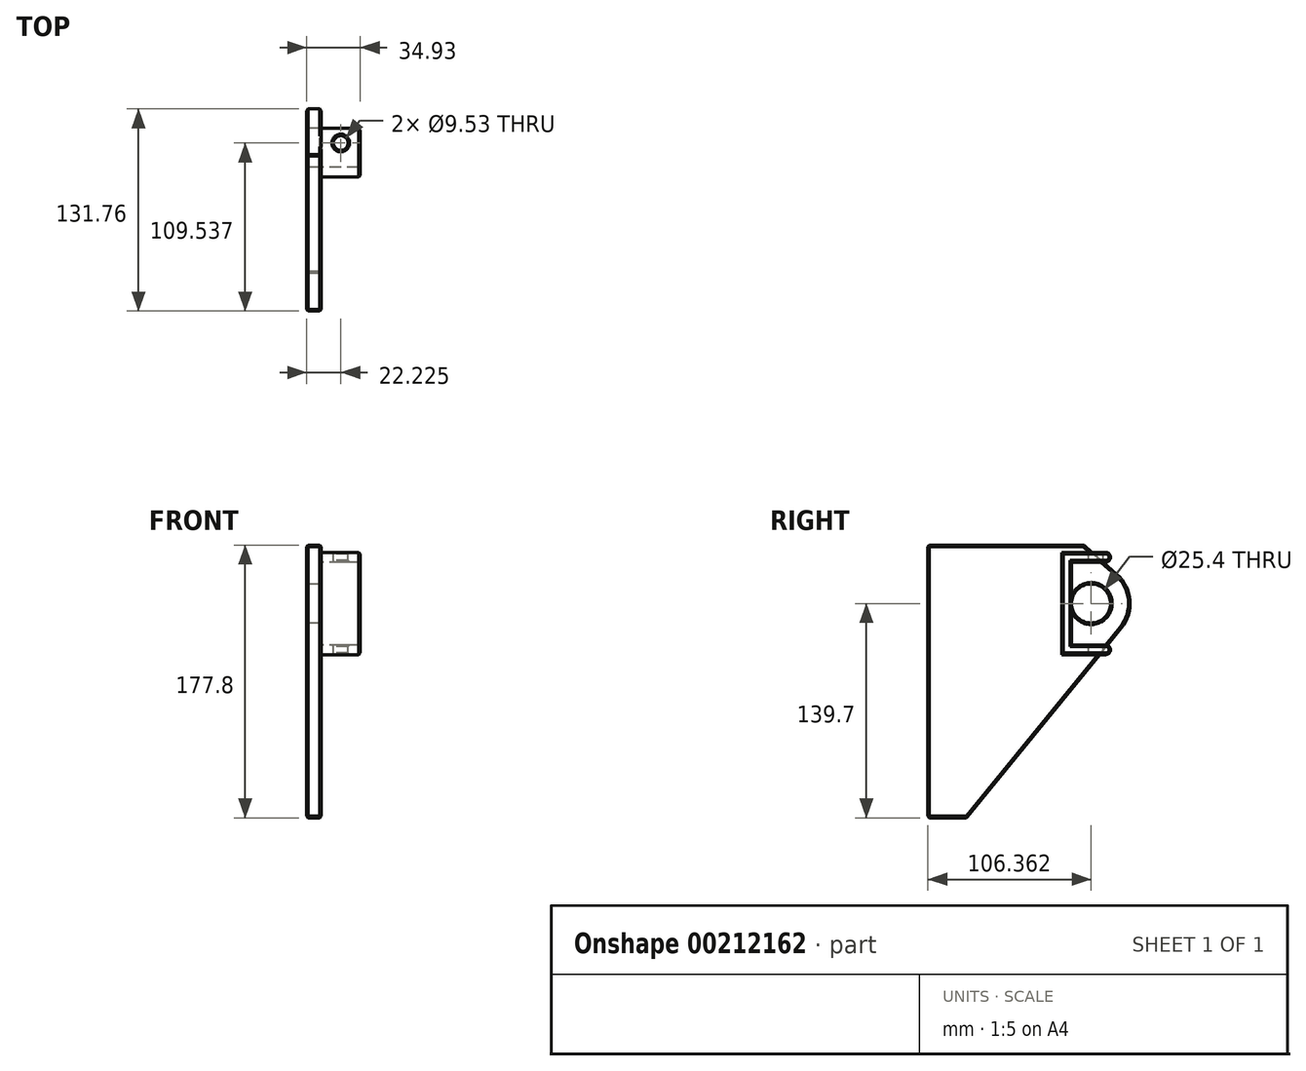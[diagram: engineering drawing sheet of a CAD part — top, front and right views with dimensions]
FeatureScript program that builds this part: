
annotation { "Feature Type Name" : "Feature", "Feature Type Description" : "" }
export const myFeature = defineFeature(function(context is Context, id is Id, definition is map)
    precondition{}
    {
        {
            var Q0;
            Q0=qCreatedBy(makeId("Right.planeOp"),FACE);
            var sketch = newSketch(context, id + "F0", { "sketchPlane" : qUnion([Q0])});
            skLineSegment(sketch, "E0", {"start": v(0, 0) * mm, "end": v(0, 177.8) * mm});
            skLineSegment(sketch, "E1", {"start": v(0, 177.8) * mm, "end": v(101.6, 177.8) * mm});
            skLineSegment(sketch, "E2", {"start": v(25.4, 0) * mm, "end": v(0, 0) * mm});
            skCircle(sketch, "E3", {"center": v(106.36, 139.7) * mm, "radius": 12.7 * mm});
            skLineSegment(sketch, "E4", {"start": v(25.4, 0) * mm, "end": v(126.06, 123.67) * mm});
            skLineSegment(sketch, "E5", {"start": v(101.6, 177.8) * mm, "end": v(123.18, 158.74) * mm});
            skArc(sketch, "E6", {"start": v(126.06, 123.67) * mm, "mid": v(131.68, 141.78) * mm, "end": v(123.18, 158.74) * mm});
            skSolve(sketch);
        }
        {
            var Q0;
            Q0=makeQuery(id+"F0.imprint","IMPRINT",FACE,{"disambiguationData":[TD([[makeQuery(id+"F0.imprint","IMPRINT",EDGE,{"derivedFrom":sQuery(id+"F0.wireOp",EDGE,"E0")}),-1.0]])]});
            extrude(context, id + "F1", {"entities" : qUnion([Q0]), "depth" : 9.52 * mm});
        }
        {
            var Q0;
            Q0=makeQuery(id+"F1.opExtrude","CAP_FACE",FACE,{"disambiguationData":[OSD([sQuery(id+"F0.wireOp",EDGE,"E0"),sQuery(id+"F0.wireOp",EDGE,"E1"),sQuery(id+"F0.wireOp",EDGE,"E2"),sQuery(id+"F0.wireOp",EDGE,"E3"),sQuery(id+"F0.wireOp",EDGE,"E4"),sQuery(id+"F0.wireOp",EDGE,"E5"),sQuery(id+"F0.wireOp",EDGE,"E6")])],"isStart":true});
            var sketch = newSketch(context, id + "F2", { "sketchPlane" : qUnion([Q0])});
            skLineSegment(sketch, "E7", {"start": v(-106.36, 139.7) * mm, "end": v(133.79, 139.7) * mm, "construction": true});
            skLineSegment(sketch, "E8", {"start": v(-106.36, 139.7) * mm, "end": v(-106.36, -37.97) * mm, "construction": true});
            skLineSegment(sketch, "E9", {"start": v(-106.36, 139.7) * mm, "end": v(-106.36, 193.68) * mm, "construction": true});
            skLineSegment(sketch, "E10", {"start": v(-131.76, 109.54) * mm, "end": v(-131.76, 109.54) * mm});
            skLineSegment(sketch, "E11", {"start": v(-135.09, 169.86) * mm, "end": v(-135.09, 169.86) * mm});
            skPoint(sketch, "E12.visualSharp", {"position": v(-135.09, 173.04) * mm});
            skPoint(sketch, "E13.visualSharp", {"position": v(-135.09, 166.69) * mm});
            skPoint(sketch, "E14.visualSharp", {"position": v(-131.76, 112.71) * mm});
            skPoint(sketch, "E15.visualSharp", {"position": v(-131.76, 106.36) * mm});
            skLineSegment(sketch, "E16", {"start": v(-93.66, 139.7) * mm, "end": v(-93.66, 166.69) * mm});
            skLineSegment(sketch, "E17", {"start": v(-93.66, 139.7) * mm, "end": v(-93.66, 112.71) * mm});
            skLineSegment(sketch, "E18.0", {"start": v(-87.31, 139.7) * mm, "end": v(-87.31, 173.04) * mm});
            skLineSegment(sketch, "E19.0", {"start": v(-87.31, 139.7) * mm, "end": v(-87.31, 106.36) * mm});
            skLineSegment(sketch, "E20", {"start": v(-87.31, 173.04) * mm, "end": v(-115.89, 173.04) * mm});
            skLineSegment(sketch, "E21.0", {"start": v(-93.66, 166.69) * mm, "end": v(-115.89, 166.69) * mm});
            skLineSegment(sketch, "E22", {"start": v(-87.31, 106.36) * mm, "end": v(-115.89, 106.36) * mm});
            skLineSegment(sketch, "E23.0", {"start": v(-93.66, 112.71) * mm, "end": v(-115.89, 112.71) * mm});
            skLineSegment(sketch, "E24", {"start": v(-119.06, 169.86) * mm, "end": v(-119.06, 169.86) * mm});
            skLineSegment(sketch, "E25", {"start": v(-119.06, 109.54) * mm, "end": v(-119.06, 109.54) * mm});
            skPoint(sketch, "E26.visualSharp", {"position": v(-119.06, 112.71) * mm});
            skArc(sketch, "E26.filletArc", {"start": v(-115.89, 112.71) * mm, "mid": v(-118.13, 111.78) * mm, "end": v(-119.06, 109.54) * mm});
            skPoint(sketch, "E27.visualSharp", {"position": v(-119.06, 106.36) * mm});
            skArc(sketch, "E27.filletArc", {"start": v(-119.06, 109.54) * mm, "mid": v(-118.13, 107.3) * mm, "end": v(-115.89, 106.36) * mm});
            skPoint(sketch, "E28.visualSharp", {"position": v(-119.06, 173.04) * mm});
            skArc(sketch, "E28.filletArc", {"start": v(-115.89, 173.04) * mm, "mid": v(-118.13, 172.1) * mm, "end": v(-119.06, 169.86) * mm});
            skPoint(sketch, "E29.visualSharp", {"position": v(-119.06, 166.69) * mm});
            skArc(sketch, "E29.filletArc", {"start": v(-119.06, 169.86) * mm, "mid": v(-118.13, 167.62) * mm, "end": v(-115.89, 166.69) * mm});
            skSolve(sketch);
        }
        {
            var Q0;
            {var subQ6=sQuery(id+"F2.wireOp",EDGE,"E16");Q0=makeQuery(id+"F2.imprint","IMPRINT",FACE,{"disambiguationData":[TD([[makeQuery(id+"F2.imprint","IMPRINT",EDGE,{"derivedFrom":subQ6}),-1.0]])]});}
            var Q1;
            {var subQ1=sQuery(id+"F2.wireOp",EDGE,"E28.filletArc");Q1=makeQuery(id+"F2.imprint","IMPRINT",FACE,{"disambiguationData":[TD([[makeQuery(id+"F2.imprint","IMPRINT",EDGE,{"derivedFrom":subQ1}),1.0]])]});}
            var Q2;
            {var subQ0=sQuery(id+"F2.wireOp",EDGE,"E27.filletArc");Q2=makeQuery(id+"F2.imprint","IMPRINT",FACE,{"disambiguationData":[TD([[makeQuery(id+"F2.imprint","IMPRINT",EDGE,{"derivedFrom":subQ0}),1.0]])]});}
            extrude(context, id + "F3", {"entities" : qUnion([Q0, Q1, Q2]), "operationType" : NewBodyOperationType.ADD, "oppositeDirection" : true, "depth" : 34.92 * mm, "hasSecondDirection" : true, "secondDirectionOppositeDirection" : true, "secondDirectionDepth" : 9.52 * mm});
        }
        {
            var Q0;
            Q0=makeQuery(id+"F3.opExtrude","SWEPT_FACE",FACE,{"disambiguationData":[OSD([sQuery(id+"F2.wireOp",EDGE,"E20")])]});
            var sketch = newSketch(context, id + "F4", { "sketchPlane" : qUnion([Q0])});
            skCircle(sketch, "E30", {"center": v(22.23, 109.54) * mm, "radius": 4.76 * mm});
            skSolve(sketch);
        }
        {
            var Q0;
            Q0=makeQuery(id+"F4.imprint","IMPRINT",FACE,{"disambiguationData":[TD([[makeQuery(id+"F4.imprint","IMPRINT",EDGE,{"derivedFrom":sQuery(id+"F4.wireOp",EDGE,"E30")}),1.0]])]});
            extrude(context, id + "F5", {"entities" : qUnion([Q0]), "operationType" : NewBodyOperationType.REMOVE, "endBound" : BoundingType.THROUGH_ALL, "oppositeDirection" : true, "depth" : 25.4 * mm});
        }
        {
            var Q0;
            Q0=makeQuery(id+"F1.opExtrude","CAP_FACE",FACE,{"disambiguationData":[OSD([sQuery(id+"F0.wireOp",EDGE,"E0"),sQuery(id+"F0.wireOp",EDGE,"E1"),sQuery(id+"F0.wireOp",EDGE,"E2"),sQuery(id+"F0.wireOp",EDGE,"E3"),sQuery(id+"F0.wireOp",EDGE,"E4"),sQuery(id+"F0.wireOp",EDGE,"E5"),sQuery(id+"F0.wireOp",EDGE,"E6")])],"isStart":true});
            var Q1;
            Q1=makeQuery(id+"F1.opExtrude","CAP_EDGE",EDGE,{"disambiguationData":[OSD([sQuery(id+"F0.wireOp",EDGE,"E3")])],"isStart":false});
            var Q2;
            Q2=makeQuery(id+"F1.opExtrude","CAP_EDGE",EDGE,{"disambiguationData":[OSD([sQuery(id+"F0.wireOp",EDGE,"E0")])],"isStart":false});
            var Q3;
            Q3=makeQuery(id+"F1.opExtrude","CAP_EDGE",EDGE,{"disambiguationData":[OSD([sQuery(id+"F0.wireOp",EDGE,"E2")])],"isStart":false});
            var Q4;
            {var subQ0=sQuery(id+"F2.wireOp",EDGE,"E22");var subQ1=sQuery(id+"F0.wireOp",EDGE,"E2");var subQ2=sQuery(id+"F0.wireOp",EDGE,"E4");Q4=makeQuery(id+"F3.boolean.opBoolean","SPLIT",EDGE,{"disambiguationData":[TD([makeQuery(id+"F1.opExtrude","CAP_FACE",FACE,{"disambiguationData":[OSD([sQuery(id+"F0.wireOp",EDGE,"E0"),sQuery(id+"F0.wireOp",EDGE,"E1"),subQ1,sQuery(id+"F0.wireOp",EDGE,"E3"),subQ2,sQuery(id+"F0.wireOp",EDGE,"E5"),sQuery(id+"F0.wireOp",EDGE,"E6")])],"isStart":false}),makeQuery(id+"F1.opExtrude","SWEPT_FACE",FACE,{"disambiguationData":[OSD([subQ1])]}),makeQuery(id+"F1.opExtrude","SWEPT_FACE",FACE,{"disambiguationData":[OSD([subQ2])]}),makeQuery(id+"F3.opExtrude","CAP_FACE",FACE,{"disambiguationData":[OSD([sQuery(id+"F2.wireOp",EDGE,"E16"),sQuery(id+"F2.wireOp",EDGE,"E17"),sQuery(id+"F2.wireOp",EDGE,"E18.0"),sQuery(id+"F2.wireOp",EDGE,"E19.0"),sQuery(id+"F2.wireOp",EDGE,"E20"),sQuery(id+"F2.wireOp",EDGE,"E21.0"),subQ0,sQuery(id+"F2.wireOp",EDGE,"E23.0"),sQuery(id+"F2.wireOp",EDGE,"E26.filletArc"),sQuery(id+"F2.wireOp",EDGE,"E27.filletArc"),sQuery(id+"F2.wireOp",EDGE,"E28.filletArc"),sQuery(id+"F2.wireOp",EDGE,"E29.filletArc")])],"isStart":true}),makeQuery(id+"F3.opExtrude","SWEPT_FACE",FACE,{"disambiguationData":[OSD([subQ0])]})])],"derivedFrom":makeQuery(id+"F1.opExtrude","CAP_EDGE",EDGE,{"disambiguationData":[OSD([subQ2])],"isStart":false})});}
            var Q5;
            Q5=makeQuery(id+"F1.opExtrude","CAP_EDGE",EDGE,{"disambiguationData":[OSD([sQuery(id+"F0.wireOp",EDGE,"E6")])],"isStart":false});
            var Q6;
            Q6=makeQuery(id+"F1.opExtrude","CAP_EDGE",EDGE,{"disambiguationData":[OSD([sQuery(id+"F0.wireOp",EDGE,"E1")])],"isStart":false});
            var Q7;
            {var subQ0=sQuery(id+"F2.wireOp",EDGE,"E20");var subQ1=sQuery(id+"F0.wireOp",EDGE,"E5");var subQ2=sQuery(id+"F0.wireOp",EDGE,"E1");Q7=makeQuery(id+"F3.boolean.opBoolean","SPLIT",EDGE,{"disambiguationData":[TD([makeQuery(id+"F1.opExtrude","CAP_FACE",FACE,{"disambiguationData":[OSD([sQuery(id+"F0.wireOp",EDGE,"E0"),subQ2,sQuery(id+"F0.wireOp",EDGE,"E2"),sQuery(id+"F0.wireOp",EDGE,"E3"),sQuery(id+"F0.wireOp",EDGE,"E4"),subQ1,sQuery(id+"F0.wireOp",EDGE,"E6")])],"isStart":false}),makeQuery(id+"F1.opExtrude","SWEPT_FACE",FACE,{"disambiguationData":[OSD([subQ2])]}),makeQuery(id+"F1.opExtrude","SWEPT_FACE",FACE,{"disambiguationData":[OSD([subQ1])]}),makeQuery(id+"F3.opExtrude","CAP_FACE",FACE,{"disambiguationData":[OSD([sQuery(id+"F2.wireOp",EDGE,"E16"),sQuery(id+"F2.wireOp",EDGE,"E17"),sQuery(id+"F2.wireOp",EDGE,"E18.0"),sQuery(id+"F2.wireOp",EDGE,"E19.0"),subQ0,sQuery(id+"F2.wireOp",EDGE,"E21.0"),sQuery(id+"F2.wireOp",EDGE,"E22"),sQuery(id+"F2.wireOp",EDGE,"E23.0"),sQuery(id+"F2.wireOp",EDGE,"E26.filletArc"),sQuery(id+"F2.wireOp",EDGE,"E27.filletArc"),sQuery(id+"F2.wireOp",EDGE,"E28.filletArc"),sQuery(id+"F2.wireOp",EDGE,"E29.filletArc")])],"isStart":true}),makeQuery(id+"F3.opExtrude","SWEPT_FACE",FACE,{"disambiguationData":[OSD([subQ0])]})])],"derivedFrom":makeQuery(id+"F1.opExtrude","CAP_EDGE",EDGE,{"disambiguationData":[OSD([subQ1])],"isStart":false})});}
            var Q8;
            Q8=makeQuery(id+"F1.opExtrude","SWEPT_EDGE",EDGE,{"disambiguationData":[OSD([sQuery(id+"F0.wireOp",EDGE,"E1"),sQuery(id+"F0.wireOp",EDGE,"E5")])]});
            var Q9;
            Q9=makeQuery(id+"F1.opExtrude","SWEPT_EDGE",EDGE,{"disambiguationData":[OSD([sQuery(id+"F0.wireOp",EDGE,"E2"),sQuery(id+"F0.wireOp",EDGE,"E4")])]});
            var Q10;
            Q10=makeQuery(id+"F1.opExtrude","SWEPT_EDGE",EDGE,{"disambiguationData":[OSD([sQuery(id+"F0.wireOp",EDGE,"E0"),sQuery(id+"F0.wireOp",EDGE,"E2")])]});
            var Q11;
            Q11=makeQuery(id+"F1.opExtrude","SWEPT_EDGE",EDGE,{"disambiguationData":[OSD([sQuery(id+"F0.wireOp",EDGE,"E0"),sQuery(id+"F0.wireOp",EDGE,"E1")])]});
            var Q12;
            Q12=makeQuery(id+"F3.opExtrude","CAP_FACE",FACE,{"disambiguationData":[OSD([sQuery(id+"F2.wireOp",EDGE,"E16"),sQuery(id+"F2.wireOp",EDGE,"E17"),sQuery(id+"F2.wireOp",EDGE,"E18.0"),sQuery(id+"F2.wireOp",EDGE,"E19.0"),sQuery(id+"F2.wireOp",EDGE,"E20"),sQuery(id+"F2.wireOp",EDGE,"E21.0"),sQuery(id+"F2.wireOp",EDGE,"E22"),sQuery(id+"F2.wireOp",EDGE,"E23.0"),sQuery(id+"F2.wireOp",EDGE,"E26.filletArc"),sQuery(id+"F2.wireOp",EDGE,"E27.filletArc"),sQuery(id+"F2.wireOp",EDGE,"E28.filletArc"),sQuery(id+"F2.wireOp",EDGE,"E29.filletArc")])],"isStart":false});
            var Q13;
            Q13=makeQuery(id+"F5.boolean.opBoolean","COPY",FACE,{"disambiguationData":[TD([makeQuery(id+"F3.opExtrude","SWEPT_FACE",FACE,{"disambiguationData":[OSD([sQuery(id+"F2.wireOp",EDGE,"E20")])]})])],"derivedFrom":makeQuery(id+"F5.opExtrude","SWEPT_FACE",FACE,{"disambiguationData":[OSD([sQuery(id+"F4.wireOp",EDGE,"E30")])]})});
            var Q14;
            Q14=makeQuery(id+"F5.boolean.opBoolean","COPY",FACE,{"disambiguationData":[TD([makeQuery(id+"F3.opExtrude","SWEPT_FACE",FACE,{"disambiguationData":[OSD([sQuery(id+"F2.wireOp",EDGE,"E22")])]})])],"derivedFrom":makeQuery(id+"F5.opExtrude","SWEPT_FACE",FACE,{"disambiguationData":[OSD([sQuery(id+"F4.wireOp",EDGE,"E30")])]})});
            chamfer(context, id + "F6", {"entities" : qUnion([Q0, Q1, Q2, Q3, Q4, Q5, Q6, Q7, Q8, Q9, Q10, Q11, Q12, Q13, Q14]), "width" : 1.02 * mm, "tangentPropagation" : true});
        }
    });
